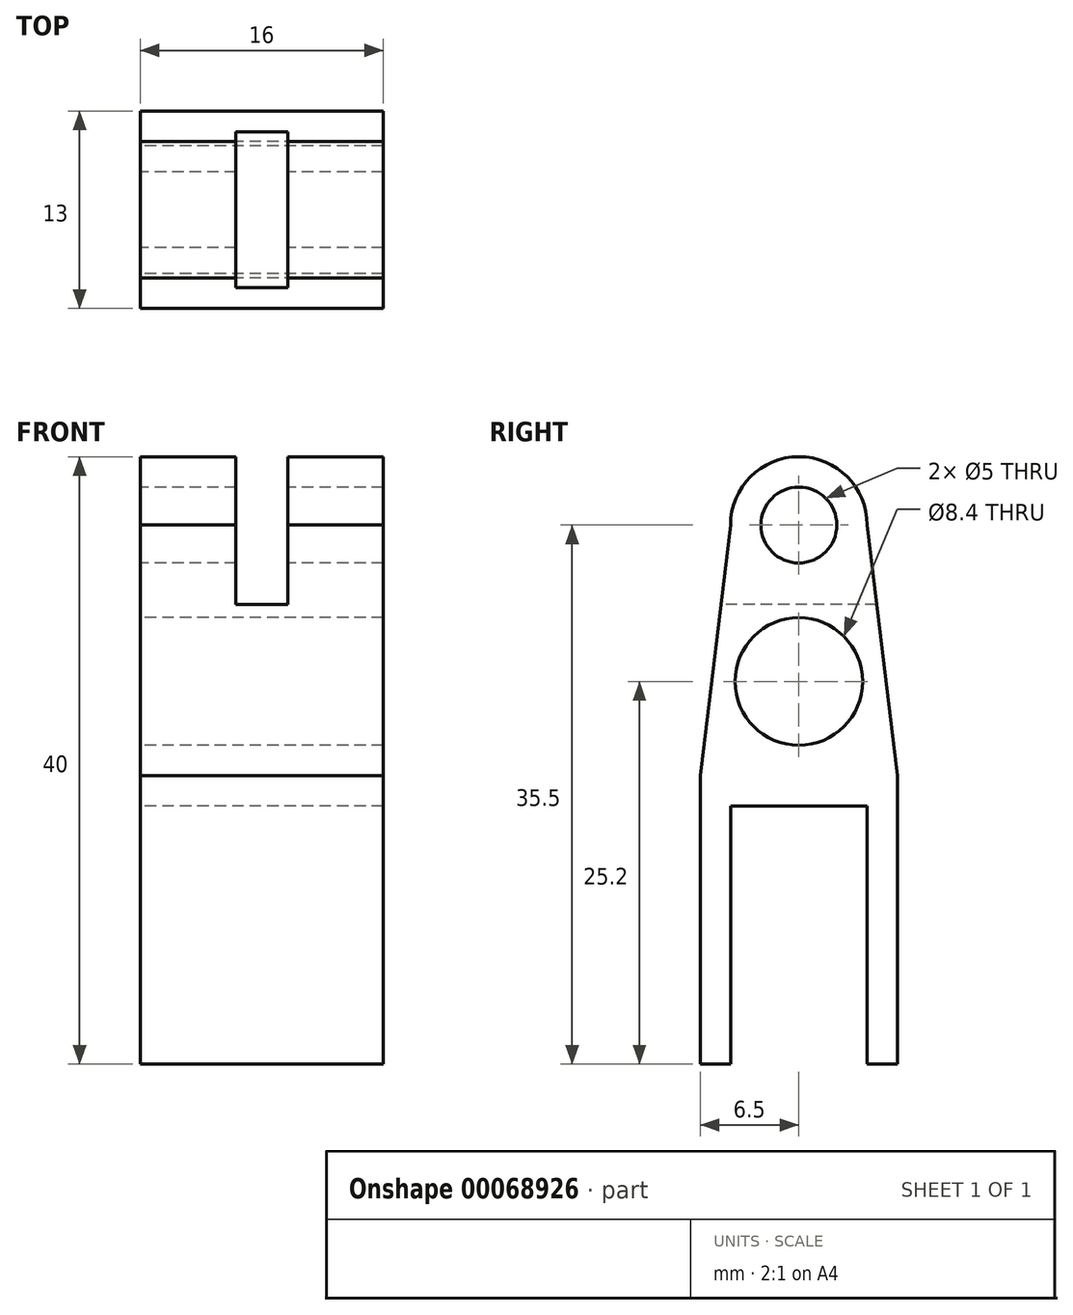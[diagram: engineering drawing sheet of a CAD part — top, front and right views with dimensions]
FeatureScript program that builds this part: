
annotation { "Feature Type Name" : "Feature", "Feature Type Description" : "" }
export const myFeature = defineFeature(function(context is Context, id is Id, definition is map)
    precondition{}
    {
        {
            var Q0;
            Q0=qCreatedBy(makeId("Right.planeOp"),FACE);
            var sketch = newSketch(context, id + "F0", { "sketchPlane" : qUnion([Q0])});
            skCircle(sketch, "E0", {"center": v(0, 0) * mm, "radius": 2.5 * mm});
            skCircle(sketch, "E1", {"center": v(0, 0) * mm, "radius": 4.5 * mm});
            skLineSegment(sketch, "E2.left", {"start": v(-6.5, -16.5) * mm, "end": v(-6.5, -35.5) * mm});
            skLineSegment(sketch, "E2.right", {"start": v(6.5, -16.5) * mm, "end": v(6.5, -35.5) * mm});
            skLineSegment(sketch, "E3.top", {"start": v(-4.5, -18.5) * mm, "end": v(4.5, -18.5) * mm});
            skLineSegment(sketch, "E3.left", {"start": v(-4.5, -35.5) * mm, "end": v(-4.5, -18.5) * mm});
            skLineSegment(sketch, "E3.right", {"start": v(4.5, -35.5) * mm, "end": v(4.5, -18.5) * mm});
            skLineSegment(sketch, "E4", {"start": v(-6.5, -35.5) * mm, "end": v(-4.5, -35.5) * mm});
            skLineSegment(sketch, "E5", {"start": v(4.5, -35.5) * mm, "end": v(6.5, -35.5) * mm});
            skLineSegment(sketch, "E6", {"start": v(0, 0.68) * mm, "end": v(0, -18.5) * mm, "construction": true});
            skLineSegment(sketch, "E7", {"start": v(-6.5, -16.5) * mm, "end": v(6.5, -16.5) * mm});
            skLineSegment(sketch, "E8", {"start": v(-4.5, 0) * mm, "end": v(-6.5, -16.5) * mm});
            skLineSegment(sketch, "E9", {"start": v(4.5, 0) * mm, "end": v(6.5, -16.5) * mm});
            skLineSegment(sketch, "E10.top", {"start": v(-6.5, -18.5) * mm, "end": v(6.5, -18.5) * mm});
            skLineSegment(sketch, "E10.left", {"start": v(-6.5, -16.5) * mm, "end": v(-6.5, -18.5) * mm});
            skLineSegment(sketch, "E10.right", {"start": v(6.5, -16.5) * mm, "end": v(6.5, -18.5) * mm});
            skCircle(sketch, "E11", {"center": v(0, -10.3) * mm, "radius": 4.2 * mm});
            skLineSegment(sketch, "E12", {"start": v(0, -5.23) * mm, "end": v(-5.13, -5.23) * mm});
            skLineSegment(sketch, "E13", {"start": v(0, -5.23) * mm, "end": v(5.13, -5.23) * mm});
            skSolve(sketch);
        }
        {
            var Q0;
            Q0 = qSketchRegion(id + "F0", true);
            extrude(context, id + "F1", {"entities" : qUnion([Q0]), "depth" : 8 * mm, "hasSecondDirection" : true, "secondDirectionOppositeDirection" : true, "secondDirectionDepth" : 8 * mm});
        }
        {
            var Q0;
            Q0=makeQuery(id+"F0.imprint","IMPRINT",FACE,{"disambiguationData":[TD([[makeQuery(id+"F0.imprint","IMPRINT",EDGE,{"derivedFrom":sQuery(id+"F0.wireOp",EDGE,"E0")}),-1.0]])]});
            var Q1;
            {var subQ0=sQuery(id+"F0.wireOp",EDGE,"E12");Q1=makeQuery(id+"F0.imprint","IMPRINT",FACE,{"disambiguationData":[TD([[makeQuery(id+"F0.imprint","IMPRINT",EDGE,{"derivedFrom":subQ0}),-1.0]])]});}
            extrude(context, id + "F2", {"entities" : qUnion([Q0, Q1]), "operationType" : NewBodyOperationType.REMOVE, "oppositeDirection" : true, "depth" : 1.7 * mm, "hasSecondDirection" : true, "secondDirectionOppositeDirection" : false, "secondDirectionDepth" : 1.7 * mm});
        }
    });
